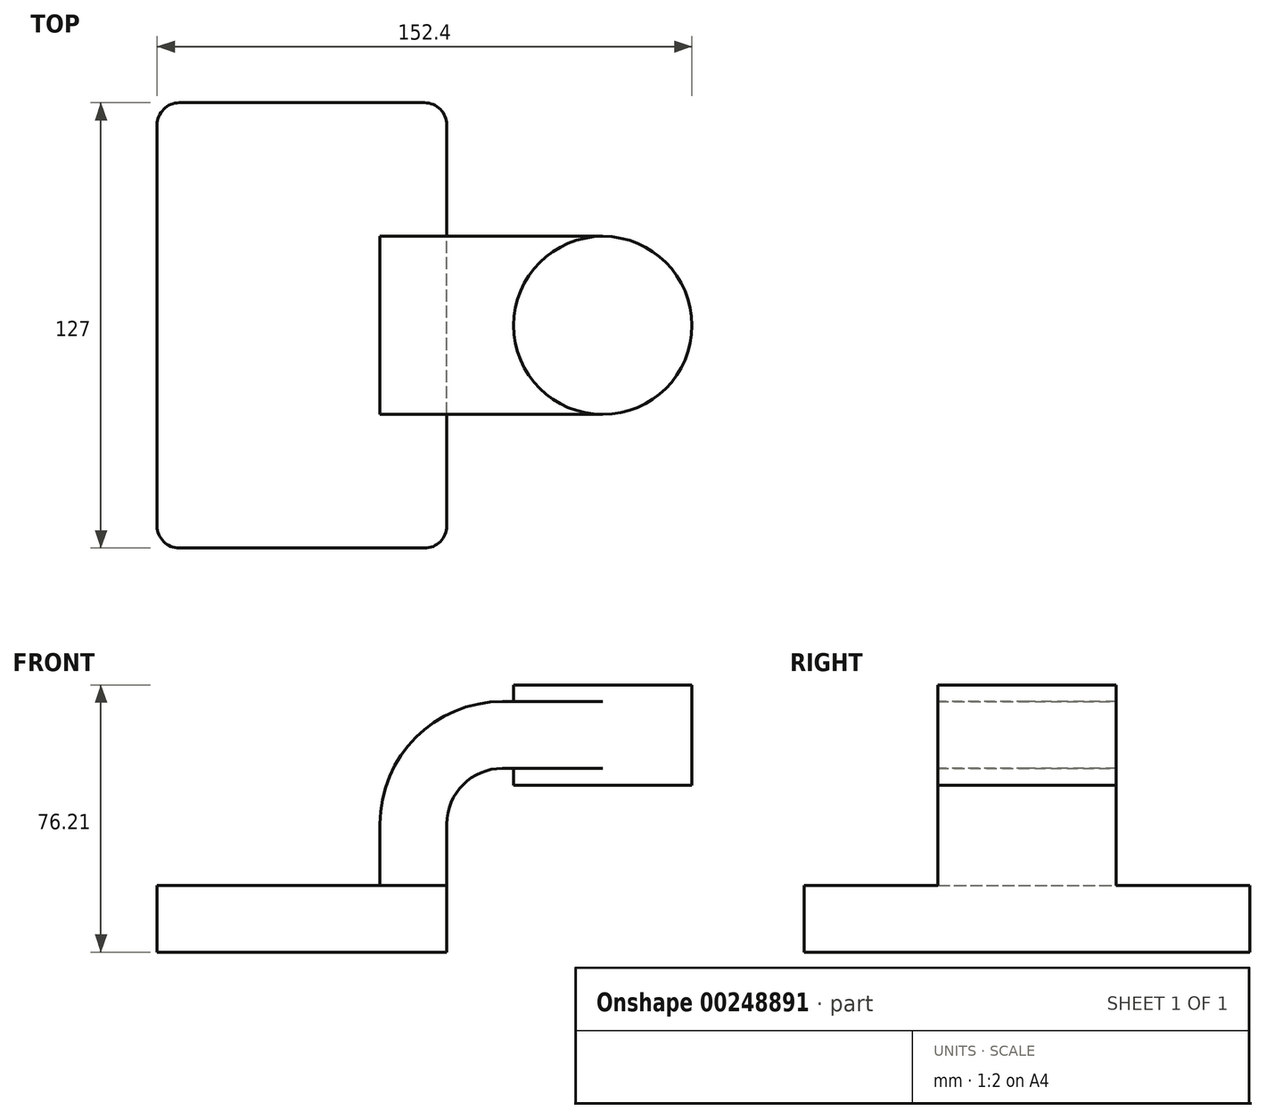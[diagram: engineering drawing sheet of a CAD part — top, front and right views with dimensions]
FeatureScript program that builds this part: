
annotation { "Feature Type Name" : "Feature", "Feature Type Description" : "" }
export const myFeature = defineFeature(function(context is Context, id is Id, definition is map)
    precondition{}
    {
        {
            var Q0;
            Q0=qCreatedBy(makeId("Front.planeOp"),FACE);
            var sketch = newSketch(context, id + "F0", { "sketchPlane" : qUnion([Q0])});
            skLineSegment(sketch, "E0.bottom", {"start": v(-41.28, 9.52) * mm, "end": v(41.27, 9.53) * mm});
            skLineSegment(sketch, "E0.top", {"start": v(-41.28, -9.52) * mm, "end": v(41.28, -9.52) * mm});
            skLineSegment(sketch, "E0.left", {"start": v(-41.28, 9.52) * mm, "end": v(-41.28, -9.53) * mm});
            skLineSegment(sketch, "E0.right", {"start": v(41.27, 9.53) * mm, "end": v(41.28, -9.52) * mm});
            skPoint(sketch, "E0.middle", {"position": v(0, 0) * mm});
            skLineSegment(sketch, "E1.bottom", {"start": v(111.12, 38.1) * mm, "end": v(60.32, 38.1) * mm});
            skLineSegment(sketch, "E1.top", {"start": v(111.12, 66.68) * mm, "end": v(60.32, 66.68) * mm});
            skLineSegment(sketch, "E1.left", {"start": v(111.12, 38.1) * mm, "end": v(111.12, 66.68) * mm});
            skLineSegment(sketch, "E1.right", {"start": v(60.32, 38.1) * mm, "end": v(60.32, 66.68) * mm});
            skPoint(sketch, "E1.middle", {"position": v(85.72, 52.39) * mm});
            skLineSegment(sketch, "E2", {"start": v(41.27, 9.53) * mm, "end": v(41.27, 27) * mm});
            skArc(sketch, "E3", {"start": v(41.27, 27) * mm, "mid": v(45.92, 38.23) * mm, "end": v(57.15, 42.88) * mm});
            skLineSegment(sketch, "E4", {"start": v(57.15, 42.88) * mm, "end": v(85.72, 42.88) * mm});
            skLineSegment(sketch, "E5.0", {"start": v(57.15, 61.93) * mm, "end": v(85.72, 61.93) * mm});
            skArc(sketch, "E5.1", {"start": v(22.22, 27) * mm, "mid": v(32.45, 51.7) * mm, "end": v(57.15, 61.93) * mm});
            skLineSegment(sketch, "E5.2", {"start": v(22.22, 9.53) * mm, "end": v(22.22, 27) * mm});
            skLineSegment(sketch, "E6", {"start": v(85.72, 38.1) * mm, "end": v(85.72, 66.68) * mm});
            skFitSpline(sketch, "E7", {"points": [v(-41.28, 9.53) * mm, v(57.15, 61.93) * mm], "startDerivative": vector(38.37, 126.05) * mm, "endDerivative": vector(145.24, -5.8) * mm});
            skSolve(sketch);
        }
        {
            var Q0;
            Q0=makeQuery(id+"F0.imprint","IMPRINT",FACE,{"disambiguationData":[TD([[makeQuery(id+"F0.imprint","IMPRINT",EDGE,{"derivedFrom":sQuery(id+"F0.wireOp",EDGE,"E0.top")}),1.0]])]});
            extrude(context, id + "F1", {"entities" : qUnion([Q0]), "endBound" : BoundingType.SYMMETRIC, "depth" : 127 * mm});
        }
        {
            var Q0;
            {var subQ1=sQuery(id+"F0.wireOp",EDGE,"E2");Q0=makeQuery(id+"F0.imprint","IMPRINT",FACE,{"disambiguationData":[TD([[makeQuery(id+"F0.imprint","IMPRINT",EDGE,{"derivedFrom":subQ1}),1.0]])]});}
            var Q1;
            {var subQ0=sQuery(id+"F0.wireOp",EDGE,"E4");var subQ1=sQuery(id+"F0.wireOp",EDGE,"E1.right");var subQ2=makeQuery(id+"F0.imprint","INTERSECT",VERTEX,{"derivedFrom":[subQ1,subQ0]});Q1=makeQuery(id+"F0.imprint","IMPRINT",FACE,{"disambiguationData":[TD([[makeQuery(id+"F0.imprint","IMPRINT",EDGE,{"disambiguationData":[TD([[subQ2,-1.0]])],"derivedFrom":subQ1}),-1.0]])]});}
            extrude(context, id + "F2", {"entities" : qUnion([Q0, Q1]), "operationType" : NewBodyOperationType.ADD, "endBound" : BoundingType.SYMMETRIC, "depth" : 50.8 * mm});
        }
        {
            var Q0;
            Q0=makeQuery(id+"F0.imprint","IMPRINT",FACE,{"disambiguationData":[TD([[makeQuery(id+"F0.imprint","IMPRINT",EDGE,{"derivedFrom":sQuery(id+"F0.wireOp",EDGE,"E5.1")}),1.0]])]});
            extrude(context, id + "F3", {"entities" : qUnion([Q0]), "operationType" : NewBodyOperationType.ADD, "depth" : 15.88 * mm});
        }
        {
            var Q0;
            {var subQ0=sQuery(id+"F0.wireOp",EDGE,"E1.left");Q0=makeQuery(id+"F0.imprint","IMPRINT",FACE,{"disambiguationData":[TD([[makeQuery(id+"F0.imprint","IMPRINT",EDGE,{"derivedFrom":subQ0}),1.0]])]});}
            var Q1;
            Q1=sQuery(id+"F0.wireOp",EDGE,"E6");
            revolve(context, id + "F4", {"operationType" : NewBodyOperationType.ADD, "entities" : qUnion([Q0]), "axis" : qUnion([Q1]), "revolveType" : RevolveType.FULL});
        }
        {
            var Q0;
            Q0=makeQuery(id+"F1.opExtrude","CAP_EDGE",EDGE,{"disambiguationData":[OSD([sQuery(id+"F0.wireOp",EDGE,"E0.left")])],"isStart":false});
            var Q1;
            Q1=makeQuery(id+"F1.opExtrude","CAP_EDGE",EDGE,{"disambiguationData":[OSD([sQuery(id+"F0.wireOp",EDGE,"E0.right")])],"isStart":false});
            var Q2;
            Q2=makeQuery(id+"F1.opExtrude","CAP_EDGE",EDGE,{"disambiguationData":[OSD([sQuery(id+"F0.wireOp",EDGE,"E0.right")])],"isStart":true});
            var Q3;
            Q3=makeQuery(id+"F1.opExtrude","CAP_EDGE",EDGE,{"disambiguationData":[OSD([sQuery(id+"F0.wireOp",EDGE,"E0.left")])],"isStart":true});
            fillet(context, id + "F5", {"entities" : qUnion([Q0, Q1, Q2, Q3]), "radius" : 6.35 * mm, "tangentPropagation" : true, "allowEdgeOverflow" : false});
        }
    });
